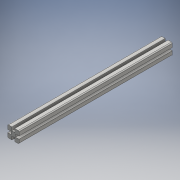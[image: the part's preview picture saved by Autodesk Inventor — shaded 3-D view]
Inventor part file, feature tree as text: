
AUTODESK INVENTOR PART (.ipt)
format: ipt  version: 2016 (Build 200138000, 138)  size: 121,344 bytes
history: native  units: mm
features: extrude x1, sketch x1
ambient origin geometry x8: Origin, YZ Plane, XZ Plane, XY Plane, X Axis, Y Axis, Z Axis, Center Point
bodies: Solid1 (feature_tree)
feature tree (2):
  extrude  "Extrusion1"  [1 undecoded]
  sketch  "Sketch1"  dims[d0=540.0mm d1=0.0mm]
note: 1 required parameter value undecoded (feature->parameter linkage not recoverable at this tier; creation-order binding heuristic only, values carry confidence <= 0.55)
